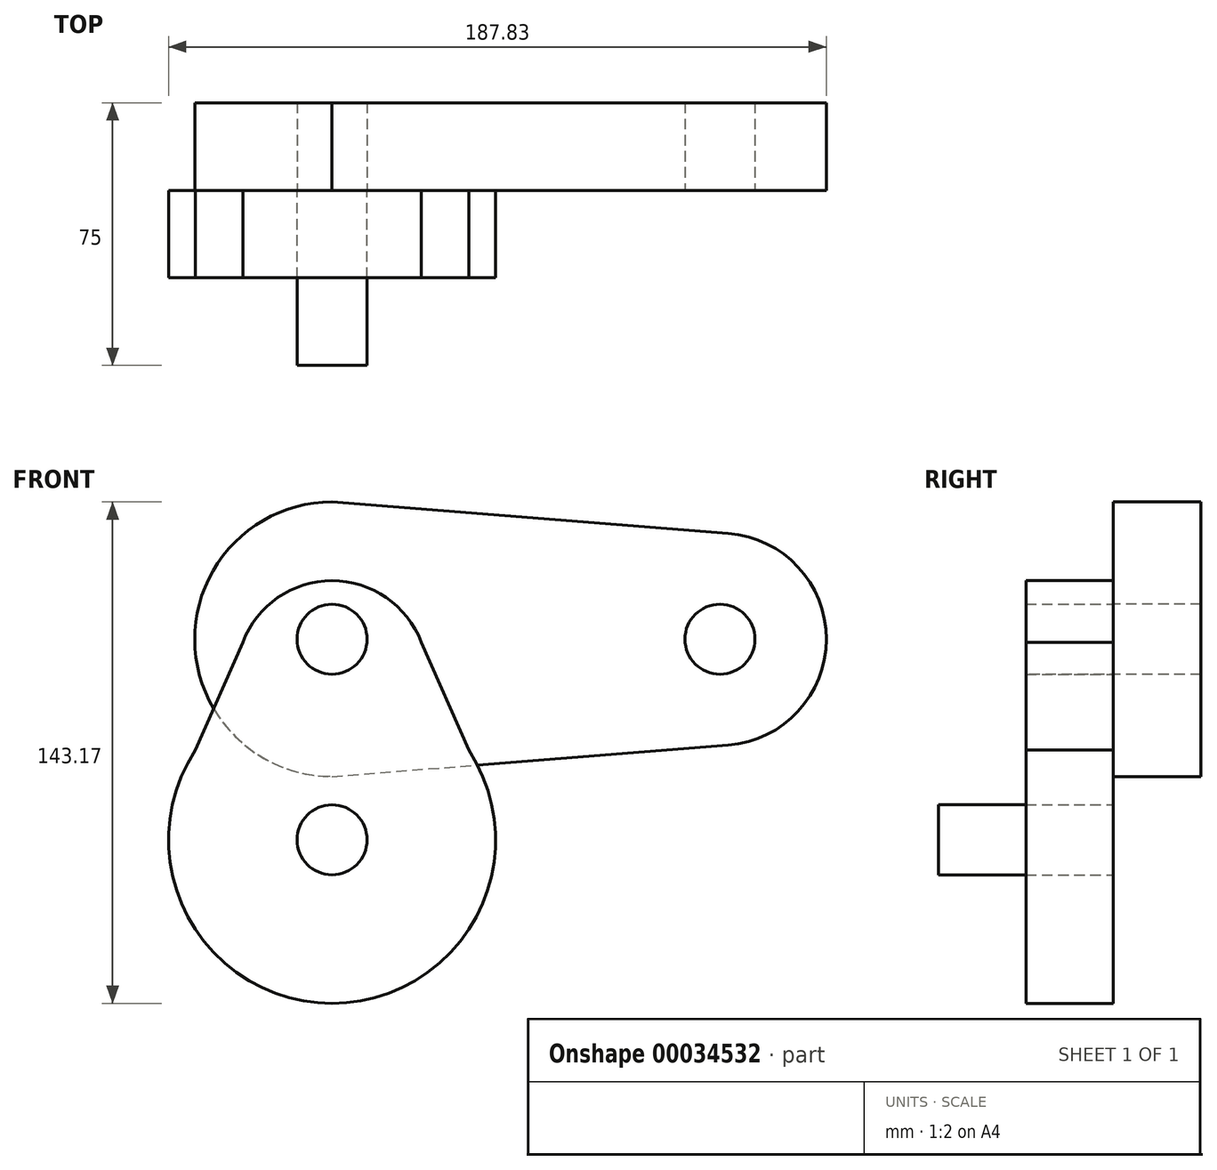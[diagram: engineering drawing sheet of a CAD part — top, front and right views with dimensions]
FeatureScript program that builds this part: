
annotation { "Feature Type Name" : "Feature", "Feature Type Description" : "" }
export const myFeature = defineFeature(function(context is Context, id is Id, definition is map)
    precondition{}
    {
        {
            var Q0;
            Q0=qCreatedBy(makeId("Front.planeOp"),FACE);
            var sketch = newSketch(context, id + "F0", { "sketchPlane" : qUnion([Q0])});
            skArc(sketch, "E0", {"start": v(0, 10) * mm, "mid": v(-10, 0) * mm, "end": v(0, -10) * mm});
            skArc(sketch, "E1", {"start": v(-39.03, 25.62) * mm, "mid": v(-41.08, -22.18) * mm, "end": v(0, -46.69) * mm});
            skLineSegment(sketch, "E2", {"start": v(-25.5, 56.43) * mm, "end": v(-39.03, 25.62) * mm});
            skLineSegment(sketch, "E3", {"start": v(0, 73.99) * mm, "end": v(0, -46.69) * mm, "construction": true});
            skArc(sketch, "E4.trimOffspring", {"start": v(0, 73.99) * mm, "mid": v(-15.48, 69.17) * mm, "end": v(-25.5, 56.43) * mm});
            skArc(sketch, "E5.MirrorCS", {"start": v(0, 73.99) * mm, "mid": v(15.48, 69.17) * mm, "end": v(25.5, 56.43) * mm});
            skLineSegment(sketch, "E6.MirrorCS", {"start": v(25.5, 56.43) * mm, "end": v(39.03, 25.62) * mm});
            skArc(sketch, "E7.MirrorCS", {"start": v(39.03, 25.62) * mm, "mid": v(41.08, -22.18) * mm, "end": v(0, -46.69) * mm});
            skArc(sketch, "E8.MirrorCS", {"start": v(0, 10) * mm, "mid": v(10, 0) * mm, "end": v(0, -10) * mm});
            skCircle(sketch, "E9", {"center": v(0, 57.28) * mm, "radius": 10 * mm});
            skSolve(sketch);
        }
        {
            var Q0;
            Q0=makeQuery(id+"F0.imprint","IMPRINT",FACE,{"disambiguationData":[TD([[makeQuery(id+"F0.imprint","IMPRINT",EDGE,{"derivedFrom":sQuery(id+"F0.wireOp",EDGE,"E0")}),-1.0]])]});
            extrude(context, id + "F1", {"entities" : qUnion([Q0]), "endBound" : BoundingType.SYMMETRIC, "depth" : 25 * mm});
        }
        {
            var Q0;
            Q0=makeQuery(id+"F1.opExtrude","CAP_FACE",FACE,{"disambiguationData":[OSD([sQuery(id+"F0.wireOp",EDGE,"E0"),sQuery(id+"F0.wireOp",EDGE,"E1"),sQuery(id+"F0.wireOp",EDGE,"E2"),sQuery(id+"F0.wireOp",EDGE,"E4.trimOffspring"),sQuery(id+"F0.wireOp",EDGE,"E5.MirrorCS"),sQuery(id+"F0.wireOp",EDGE,"E6.MirrorCS"),sQuery(id+"F0.wireOp",EDGE,"E7.MirrorCS"),sQuery(id+"F0.wireOp",EDGE,"E8.MirrorCS"),sQuery(id+"F0.wireOp",EDGE,"E9")])],"isStart":true});
            var sketch = newSketch(context, id + "F2", { "sketchPlane" : qUnion([Q0])});
            skCircle(sketch, "E10.0", {"center": v(0, 57.28) * mm, "radius": 10 * mm});
            skSolve(sketch);
        }
        {
            var Q0;
            Q0 = qSketchRegion(id + "F2", true);
            extrude(context, id + "F3", {"entities" : qUnion([Q0]), "endBound" : BoundingType.SYMMETRIC, "depth" : 50 * mm});
        }
        {
            var Q0;
            Q0=makeQuery(id+"F1.opExtrude","CAP_FACE",FACE,{"disambiguationData":[OSD([sQuery(id+"F0.wireOp",EDGE,"E0"),sQuery(id+"F0.wireOp",EDGE,"E1"),sQuery(id+"F0.wireOp",EDGE,"E2"),sQuery(id+"F0.wireOp",EDGE,"E4.trimOffspring"),sQuery(id+"F0.wireOp",EDGE,"E5.MirrorCS"),sQuery(id+"F0.wireOp",EDGE,"E6.MirrorCS"),sQuery(id+"F0.wireOp",EDGE,"E7.MirrorCS"),sQuery(id+"F0.wireOp",EDGE,"E8.MirrorCS"),sQuery(id+"F0.wireOp",EDGE,"E9")])],"isStart":true});
            var sketch = newSketch(context, id + "F4", { "sketchPlane" : qUnion([Q0])});
            skCircle(sketch, "E11.0", {"center": v(0, 57.28) * mm, "radius": 10 * mm});
            skArc(sketch, "E12", {"start": v(-6.16, 18.57) * mm, "mid": v(39.2, 57.28) * mm, "end": v(-6.16, 96) * mm});
            skLineSegment(sketch, "E13", {"start": v(0, 57.28) * mm, "end": v(-110.79, 57.28) * mm, "construction": true});
            skArc(sketch, "E14", {"start": v(-113.18, 87.54) * mm, "mid": v(-141.14, 57.28) * mm, "end": v(-113.18, 27.03) * mm});
            skLineSegment(sketch, "E15", {"start": v(0, 96.48) * mm, "end": v(-113.18, 87.54) * mm});
            skLineSegment(sketch, "E16", {"start": v(0, 18.09) * mm, "end": v(-113.18, 27.03) * mm});
            skCircle(sketch, "E17", {"center": v(-110.79, 57.28) * mm, "radius": 10 * mm});
            skSolve(sketch);
        }
        {
            var Q0;
            {var subQ8=sQuery(id+"F4.wireOp",EDGE,"E14");Q0=makeQuery(id+"F4.imprint","IMPRINT",FACE,{"disambiguationData":[TD([[makeQuery(id+"F4.imprint","IMPRINT",EDGE,{"derivedFrom":subQ8}),1.0]])]});}
            var Q1;
            Q1=makeQuery(id+"F4.imprint","IMPRINT",FACE,{"disambiguationData":[TD([[makeQuery(id+"F4.imprint","IMPRINT",EDGE,{"derivedFrom":sQuery(id+"F4.wireOp",EDGE,"E11.0")}),1.0]])]});
            extrude(context, id + "F5", {"entities" : qUnion([Q0, Q1]), "depth" : 25 * mm});
        }
        {
            var Q0;
            Q0=makeQuery(id+"F1.opExtrude","CAP_FACE",FACE,{"disambiguationData":[OSD([sQuery(id+"F0.wireOp",EDGE,"E0"),sQuery(id+"F0.wireOp",EDGE,"E1"),sQuery(id+"F0.wireOp",EDGE,"E2"),sQuery(id+"F0.wireOp",EDGE,"E4.trimOffspring"),sQuery(id+"F0.wireOp",EDGE,"E5.MirrorCS"),sQuery(id+"F0.wireOp",EDGE,"E6.MirrorCS"),sQuery(id+"F0.wireOp",EDGE,"E7.MirrorCS"),sQuery(id+"F0.wireOp",EDGE,"E8.MirrorCS"),sQuery(id+"F0.wireOp",EDGE,"E9")])],"isStart":false});
            var sketch = newSketch(context, id + "F6", { "sketchPlane" : qUnion([Q0])});
            skCircle(sketch, "E18.0", {"center": v(0, 0) * mm, "radius": 10 * mm});
            skSolve(sketch);
        }
        {
            var Q0;
            Q0 = qSketchRegion(id + "F6", true);
            extrude(context, id + "F7", {"entities" : qUnion([Q0]), "endBound" : BoundingType.SYMMETRIC, "depth" : 50 * mm});
        }
    });
